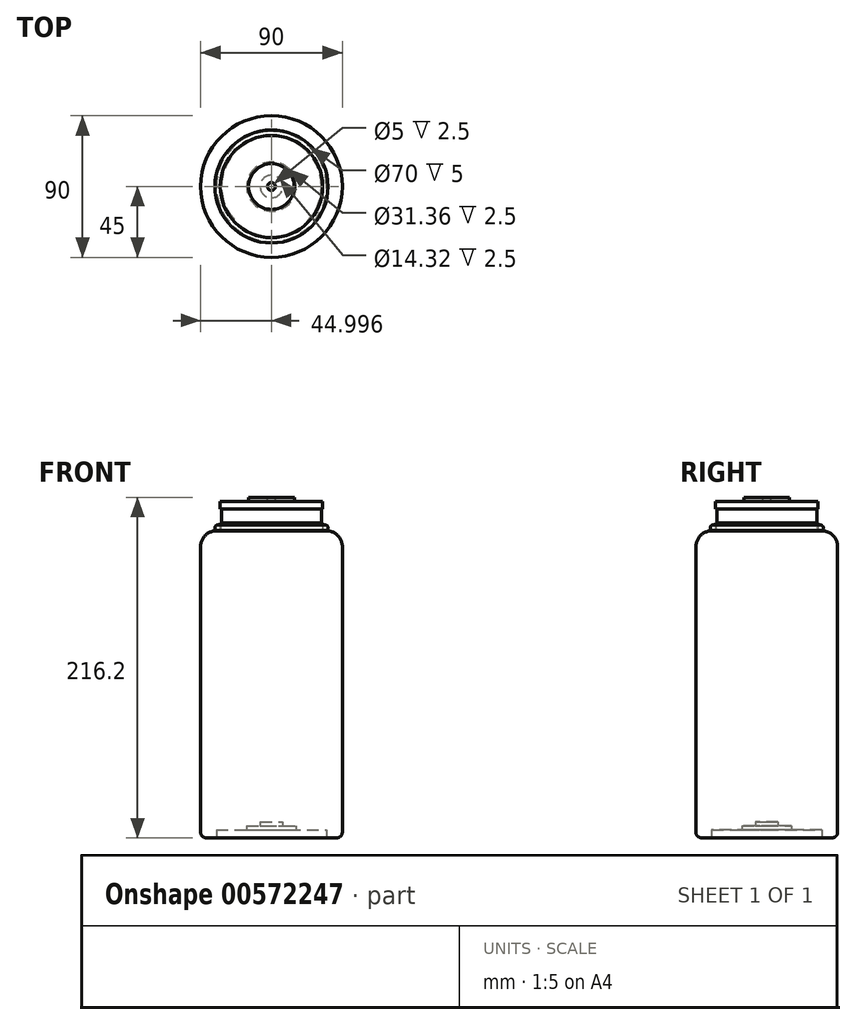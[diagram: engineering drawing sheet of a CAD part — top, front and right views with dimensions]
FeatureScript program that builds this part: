
annotation { "Feature Type Name" : "Feature", "Feature Type Description" : "" }
export const myFeature = defineFeature(function(context is Context, id is Id, definition is map)
    precondition{}
    {
        {
            var Q0;
            Q0=qCreatedBy(makeId("Front.planeOp"),FACE);
            var sketch = newSketch(context, id + "F0", { "sketchPlane" : qUnion([Q0])});
            skLineSegment(sketch, "E0", {"start": v(60.69, -74.18) * mm, "end": v(60.69, 120.82) * mm});
            skLineSegment(sketch, "E1", {"start": v(60.69, 120.82) * mm, "end": v(15.69, 120.82) * mm});
            skLineSegment(sketch, "E2", {"start": v(15.69, 120.82) * mm, "end": v(15.69, -74.18) * mm});
            skLineSegment(sketch, "E3", {"start": v(15.69, -74.18) * mm, "end": v(60.69, -74.18) * mm});
            skSolve(sketch);
        }
        {
            var Q0;
            Q0=makeQuery(id+"F0.imprint","IMPRINT",FACE,{"disambiguationData":[TD([[makeQuery(id+"F0.imprint","IMPRINT",EDGE,{"derivedFrom":sQuery(id+"F0.wireOp",EDGE,"E0")}),1.0]])]});
            var Q1;
            Q1=sQuery(id+"F0.wireOp",EDGE,"E2");
            revolve(context, id + "F1", {"entities" : qUnion([Q0]), "axis" : qUnion([Q1]), "revolveType" : RevolveType.FULL});
        }
        {
            var Q0;
            Q0=makeQuery(id+"F1.opRevolve","SWEPT_FACE",FACE,{"disambiguationData":[OSD([sQuery(id+"F0.wireOp",EDGE,"E1")])]});
            fillet(context, id + "F2", {"entities" : qUnion([Q0]), "radius" : 10 * mm, "tangentPropagation" : true, "allowEdgeOverflow" : false});
        }
        {
            var Q0;
            Q0=makeQuery(id+"F1.opRevolve","SWEPT_FACE",FACE,{"disambiguationData":[OSD([sQuery(id+"F0.wireOp",EDGE,"E3")])]});
            var sketch = newSketch(context, id + "F3", { "sketchPlane" : qUnion([Q0])});
            skCircle(sketch, "E4", {"center": v(15.69, 0) * mm, "radius": 35 * mm});
            skSolve(sketch);
        }
        {
            var Q0;
            Q0=makeQuery(id+"F3.imprint","IMPRINT",FACE,{"disambiguationData":[TD([[makeQuery(id+"F3.imprint","IMPRINT",EDGE,{"derivedFrom":sQuery(id+"F3.wireOp",EDGE,"E4")}),1.0]])]});
            extrude(context, id + "F4", {"entities" : qUnion([Q0]), "operationType" : NewBodyOperationType.REMOVE, "oppositeDirection" : true, "depth" : 5 * mm, "offsetDistance" : 25 * mm});
        }
        {
            var Q0;
            Q0=makeQuery(id+"F4.boolean.opBoolean","COPY",FACE,{"derivedFrom":makeQuery(id+"F4.opExtrude","CAP_FACE",FACE,{"disambiguationData":[OSD([sQuery(id+"F3.wireOp",EDGE,"E4")])],"isStart":false})});
            var sketch = newSketch(context, id + "F5", { "sketchPlane" : qUnion([Q0])});
            skCircle(sketch, "E5", {"center": v(15.69, 0) * mm, "radius": 15.68 * mm});
            skCircle(sketch, "E6", {"center": v(15.69, 0) * mm, "radius": 7.16 * mm});
            skSolve(sketch);
        }
        {
            var Q0;
            Q0=makeQuery(id+"F5.imprint","IMPRINT",FACE,{"disambiguationData":[TD([[makeQuery(id+"F5.imprint","IMPRINT",EDGE,{"derivedFrom":sQuery(id+"F5.wireOp",EDGE,"E6")}),1.0]])]});
            extrude(context, id + "F6", {"entities" : qUnion([Q0]), "operationType" : NewBodyOperationType.REMOVE, "oppositeDirection" : true, "depth" : 5 * mm, "offsetDistance" : 25 * mm});
        }
        {
            var Q0;
            Q0=makeQuery(id+"F5.imprint","IMPRINT",FACE,{"disambiguationData":[TD([[makeQuery(id+"F5.imprint","IMPRINT",EDGE,{"derivedFrom":sQuery(id+"F5.wireOp",EDGE,"E5")}),1.0]])]});
            extrude(context, id + "F7", {"entities" : qUnion([Q0]), "operationType" : NewBodyOperationType.REMOVE, "oppositeDirection" : true, "depth" : 2.5 * mm, "offsetDistance" : 25 * mm});
        }
        {
            var Q0;
            Q0=qCreatedBy(makeId("Front.planeOp"),FACE);
            var sketch = newSketch(context, id + "F8", { "sketchPlane" : qUnion([Q0])});
            skCircle(sketch, "E7", {"center": v(49.78, 122.78) * mm, "radius": 1.8 * mm});
            skSolve(sketch);
        }
        {
            var Q0;
            Q0=makeQuery(id+"F1.opRevolve","SWEPT_FACE",FACE,{"disambiguationData":[OSD([sQuery(id+"F0.wireOp",EDGE,"E1")])]});
            var sketch = newSketch(context, id + "F9", { "sketchPlane" : qUnion([Q0])});
            skCircle(sketch, "E8", {"center": v(15.69, 0) * mm, "radius": 35 * mm});
            skSolve(sketch);
        }
        {
            var Q0;
            Q0=makeQuery(id+"F8.imprint","IMPRINT",FACE,{"disambiguationData":[TD([[makeQuery(id+"F8.imprint","IMPRINT",EDGE,{"derivedFrom":sQuery(id+"F8.wireOp",EDGE,"E7")}),1.0]])]});
            var Q1;
            Q1=sQuery(id+"F9.wireOp",EDGE,"E8");
            sweep(context, id + "F10", {"profiles" : qUnion([Q0]), "path" : qUnion([Q1])});
        }
        {
            var Q0;
            Q0=makeQuery(id+"F1.opRevolve","SWEPT_FACE",FACE,{"disambiguationData":[OSD([sQuery(id+"F0.wireOp",EDGE,"E1")])]});
            var sketch = newSketch(context, id + "F11", { "sketchPlane" : qUnion([Q0])});
            skCircle(sketch, "E9", {"center": v(15.69, 0) * mm, "radius": 32.5 * mm});
            skSolve(sketch);
        }
        {
            var Q0;
            Q0=makeQuery(id+"F11.imprint","IMPRINT",FACE,{"disambiguationData":[TD([[makeQuery(id+"F11.imprint","IMPRINT",EDGE,{"derivedFrom":sQuery(id+"F11.wireOp",EDGE,"E9")}),1.0]])]});
            extrude(context, id + "F12", {"entities" : qUnion([Q0]), "depth" : 5 * mm, "offsetDistance" : 25 * mm});
        }
        {
            var Q0;
            Q0=makeQuery(id+"F12.opExtrude","CAP_FACE",FACE,{"disambiguationData":[OSD([sQuery(id+"F11.wireOp",EDGE,"E9")])],"isStart":false});
            var sketch = newSketch(context, id + "F13", { "sketchPlane" : qUnion([Q0])});
            skCircle(sketch, "E10", {"center": v(15.69, 0) * mm, "radius": 31.75 * mm});
            skSolve(sketch);
        }
        {
            var Q0;
            Q0 = qSketchRegion(id + "F13", true);
            extrude(context, id + "F14", {"entities" : qUnion([Q0]), "operationType" : NewBodyOperationType.ADD, "depth" : 9 * mm, "offsetDistance" : 25 * mm});
        }
        {
            var Q0;
            Q0=makeQuery(id+"F14.opExtrude","CAP_FACE",FACE,{"disambiguationData":[OSD([sQuery(id+"F13.wireOp",EDGE,"E10")])],"isStart":false});
            var sketch = newSketch(context, id + "F15", { "sketchPlane" : qUnion([Q0])});
            skCircle(sketch, "E11", {"center": v(15.69, 0) * mm, "radius": 32.5 * mm});
            skSolve(sketch);
        }
        {
            var Q0;
            Q0 = qSketchRegion(id + "F15", true);
            extrude(context, id + "F16", {"entities" : qUnion([Q0]), "depth" : 4.5 * mm, "offsetDistance" : 25 * mm});
        }
        {
            var Q0;
            Q0=makeQuery(id+"F16.opExtrude","CAP_FACE",FACE,{"disambiguationData":[OSD([sQuery(id+"F15.wireOp",EDGE,"E11")])],"isStart":false});
            var sketch = newSketch(context, id + "F17", { "sketchPlane" : qUnion([Q0])});
            skCircle(sketch, "E12", {"center": v(15.69, 0) * mm, "radius": 14.5 * mm});
            skSolve(sketch);
        }
        {
            var Q0;
            Q0 = qSketchRegion(id + "F17", true);
            extrude(context, id + "F18", {"entities" : qUnion([Q0]), "depth" : 2.7 * mm, "offsetDistance" : 25 * mm});
        }
        {
            var Q0;
            Q0=makeQuery(id+"F18.opExtrude","CAP_FACE",FACE,{"disambiguationData":[OSD([sQuery(id+"F17.wireOp",EDGE,"E12")])],"isStart":false});
            var sketch = newSketch(context, id + "F19", { "sketchPlane" : qUnion([Q0])});
            skCircle(sketch, "E13", {"center": v(15.69, 0) * mm, "radius": 2.5 * mm});
            skSolve(sketch);
        }
        {
            var Q0;
            Q0=makeQuery(id+"F19.imprint","IMPRINT",FACE,{"disambiguationData":[TD([[makeQuery(id+"F19.imprint","IMPRINT",EDGE,{"derivedFrom":sQuery(id+"F19.wireOp",EDGE,"E13")}),1.0]])]});
            var Q1;
            Q1=sQuery(id+"F19.wireOp",EDGE,"E13");
            extrude(context, id + "F20", {"entities" : qUnion([Q0]), "operationType" : NewBodyOperationType.REMOVE, "surfaceEntities" : qUnion([Q1]), "oppositeDirection" : true, "depth" : 2.5 * mm, "offsetDistance" : 25 * mm});
        }
        {
            var Q0;
            Q0=makeQuery(id+"F1.opRevolve","SWEPT_EDGE",EDGE,{"disambiguationData":[OSD([sQuery(id+"F0.wireOp",EDGE,"E0"),sQuery(id+"F0.wireOp",EDGE,"E3")])]});
            fillet(context, id + "F21", {"entities" : qUnion([Q0]), "radius" : 3.5 * mm, "tangentPropagation" : true, "allowEdgeOverflow" : false});
        }
        {
            var Q0;
            Q0=qCreatedBy(makeId("Front.planeOp"),FACE);
            var sketch = newSketch(context, id + "F22", { "sketchPlane" : qUnion([Q0])});
            skArc(sketch, "E14", {"start": v(54.07, 160.54) * mm, "mid": v(33.07, 156.43) * mm, "end": v(16.44, 142.95) * mm});
            skArc(sketch, "E15", {"start": v(51.5, 121.09) * mm, "mid": v(72.51, 139.53) * mm, "end": v(54.07, 160.54) * mm});
            skArc(sketch, "E16.0", {"start": v(53.96, 158.55) * mm, "mid": v(33.9, 154.61) * mm, "end": v(18.04, 141.75) * mm});
            skArc(sketch, "E16.1", {"start": v(51.63, 123.08) * mm, "mid": v(70.52, 139.65) * mm, "end": v(53.96, 158.55) * mm});
            skLineSegment(sketch, "E17", {"start": v(18.04, 141.75) * mm, "end": v(16.44, 142.95) * mm});
            skLineSegment(sketch, "E18", {"start": v(51.5, 121.09) * mm, "end": v(51.63, 123.08) * mm});
            skSolve(sketch);
        }
        {
            var Q0;
            Q0=sQuery(id+"F22.wireOp",EDGE,"E14");
            var Q1;
            Q1=sQuery(id+"F22.wireOp",EDGE,"E15");
            var Q2;
            Q2=makeQuery(id+"F1.opRevolve","SWEPT_FACE",FACE,{"disambiguationData":[OSD([sQuery(id+"F0.wireOp",EDGE,"E0")])]});
            revolve(context, id + "F23", {"bodyType" : ToolBodyType.SURFACE, "surfaceEntities" : qUnion([Q0, Q1]), "axis" : qUnion([Q2]), "revolveType" : RevolveType.ONE_DIRECTION, "angle" : 25 * degree});
        }
    });
